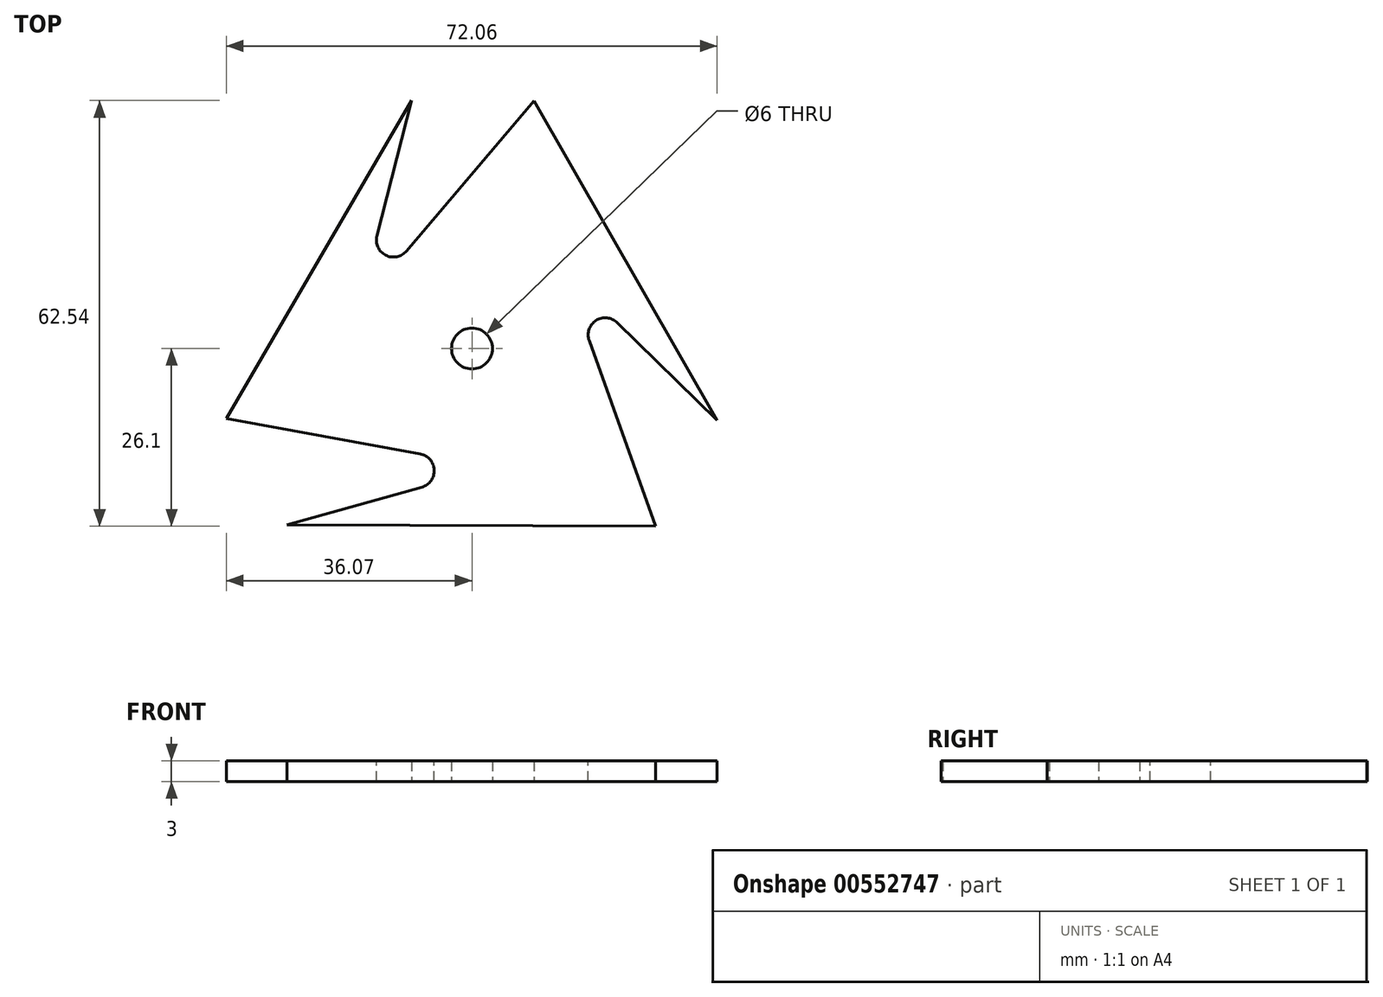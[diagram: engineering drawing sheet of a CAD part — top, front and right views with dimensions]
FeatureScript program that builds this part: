
annotation { "Feature Type Name" : "Feature", "Feature Type Description" : "" }
export const myFeature = defineFeature(function(context is Context, id is Id, definition is map)
    precondition{}
    {
        {
            var Q0;
            Q0=qCreatedBy(makeId("Top.planeOp"),FACE);
            var sketch = newSketch(context, id + "F0", { "sketchPlane" : qUnion([Q0])});
            skLineSegment(sketch, "E0.bottom", {"start": v(0, 0) * mm, "end": v(75, 0) * mm, "construction": true});
            skLineSegment(sketch, "E0.top", {"start": v(0, 75) * mm, "end": v(75, 75) * mm, "construction": true});
            skLineSegment(sketch, "E0.left", {"start": v(0, 0) * mm, "end": v(0, 75) * mm, "construction": true});
            skLineSegment(sketch, "E0.right", {"start": v(75, 0) * mm, "end": v(75, 75) * mm, "construction": true});
            skLineSegment(sketch, "E1", {"start": v(0, 75) * mm, "end": v(75, 0) * mm, "construction": true});
            skCircle(sketch, "E2", {"center": v(37.5, 37.5) * mm, "radius": 3 * mm});
            skCircle(sketch, "E3", {"center": v(37.5, 37.5) * mm, "radius": 37.5 * mm});
            skLineSegment(sketch, "E4", {"start": v(1.43, 27.23) * mm, "end": v(40.55, 20.06) * mm});
            skLineSegment(sketch, "E5", {"start": v(40.55, 20.06) * mm, "end": v(10.37, 11.6) * mm});
            skLineSegment(sketch, "E6.1.0", {"start": v(51.08, 48.86) * mm, "end": v(73.49, 26.95) * mm});
            skLineSegment(sketch, "E6.1.1", {"start": v(64.43, 11.4) * mm, "end": v(51.08, 48.86) * mm});
            skLineSegment(sketch, "E6.2.0", {"start": v(20.87, 43.58) * mm, "end": v(28.64, 73.94) * mm});
            skLineSegment(sketch, "E6.2.1", {"start": v(46.64, 73.87) * mm, "end": v(20.87, 43.58) * mm});
            skLineSegment(sketch, "E7", {"start": v(28.64, 73.94) * mm, "end": v(1.43, 27.23) * mm});
            skLineSegment(sketch, "E8", {"start": v(10.37, 11.6) * mm, "end": v(64.43, 11.4) * mm});
            skLineSegment(sketch, "E9", {"start": v(46.64, 73.87) * mm, "end": v(73.49, 26.95) * mm});
            skSolve(sketch);
        }
        {
            var Q0;
            Q0=makeQuery(id+"F0.imprint","IMPRINT",FACE,{"disambiguationData":[TD([[makeQuery(id+"F0.imprint","IMPRINT",EDGE,{"derivedFrom":sQuery(id+"F0.wireOp",EDGE,"E2")}),-1.0]])]});
            extrude(context, id + "F1", {"entities" : qUnion([Q0]), "depth" : 3 * mm, "offsetDistance" : 25 * mm});
        }
        {
            var Q0;
            Q0 = qSketchRegion(id + "FcyLruim4WYMqyl_0", true);
            var Q1;
            Q1=makeQuery(id+"F0.imprint","IMPRINT",FACE,{"disambiguationData":[TD([[makeQuery(id+"F0.imprint","IMPRINT",EDGE,{"derivedFrom":sQuery(id+"F0.wireOp",EDGE,"E2")}),-1.0]])]});
            extrude(context, id + "F2", {"entities" : qUnion([Q0, Q1]), "operationType" : NewBodyOperationType.ADD, "depth" : 3 * mm, "offsetDistance" : 25 * mm});
        }
        {
            var Q0;
            Q0=makeQuery(id+"F1.opExtrude","SWEPT_EDGE",EDGE,{"disambiguationData":[OSD([sQuery(id+"F0.wireOp",EDGE,"E6.1.0"),sQuery(id+"F0.wireOp",EDGE,"E6.1.1")])]});
            fillet(context, id + "F3", {"entities" : qUnion([Q0]), "radius" : 2.5 * mm, "tangentPropagation" : true, "allowEdgeOverflow" : false});
        }
        {
            var Q0;
            Q0=makeQuery(id+"F1.opExtrude","SWEPT_EDGE",EDGE,{"disambiguationData":[OSD([sQuery(id+"F0.wireOp",EDGE,"E6.2.0"),sQuery(id+"F0.wireOp",EDGE,"E6.2.1")])]});
            fillet(context, id + "F4", {"entities" : qUnion([Q0]), "radius" : 2.5 * mm, "tangentPropagation" : true, "allowEdgeOverflow" : false});
        }
        {
            var Q0;
            Q0=makeQuery(id+"F1.opExtrude","SWEPT_EDGE",EDGE,{"disambiguationData":[OSD([sQuery(id+"F0.wireOp",EDGE,"E4"),sQuery(id+"F0.wireOp",EDGE,"E5")])]});
            fillet(context, id + "F5", {"entities" : qUnion([Q0]), "radius" : 2.5 * mm, "tangentPropagation" : true, "allowEdgeOverflow" : false});
        }
    });
